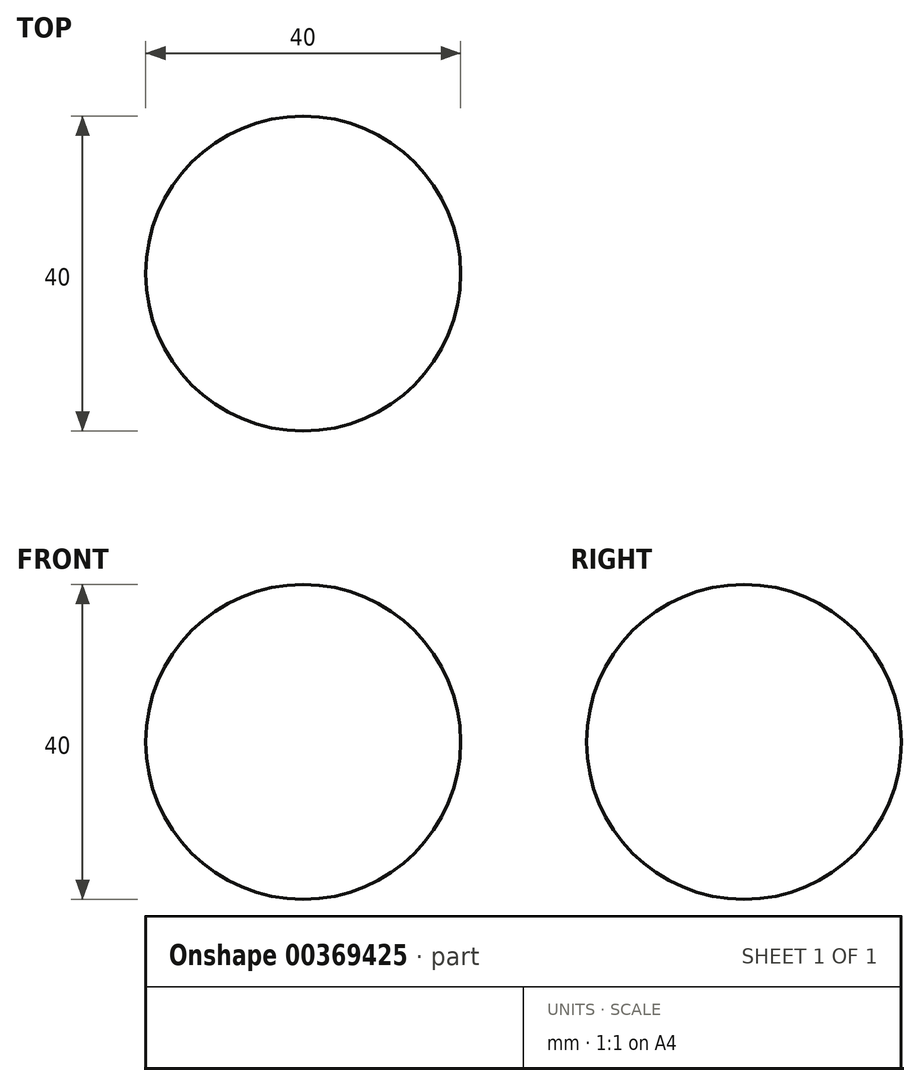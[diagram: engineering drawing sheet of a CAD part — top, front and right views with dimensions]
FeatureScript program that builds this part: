
annotation { "Feature Type Name" : "Feature", "Feature Type Description" : "" }
export const myFeature = defineFeature(function(context is Context, id is Id, definition is map)
    precondition{}
    {
        {
            var Q0;
            Q0=qCreatedBy(makeId("Front.planeOp"),FACE);
            var sketch = newSketch(context, id + "F0", { "sketchPlane" : qUnion([Q0])});
            skLineSegment(sketch, "E0", {"start": v(0, 0) * mm, "end": v(0, 40) * mm});
            skArc(sketch, "E1", {"start": v(0, 0) * mm, "mid": v(20, 20) * mm, "end": v(0, 40) * mm});
            skSolve(sketch);
        }
        {
            var Q0;
            Q0 = qSketchRegion(id + "F0", true);
            var Q1;
            Q1=sQuery(id+"F0.wireOp",EDGE,"E0");
            revolve(context, id + "F1", {"entities" : qUnion([Q0]), "axis" : qUnion([Q1]), "revolveType" : RevolveType.FULL});
        }
    });
